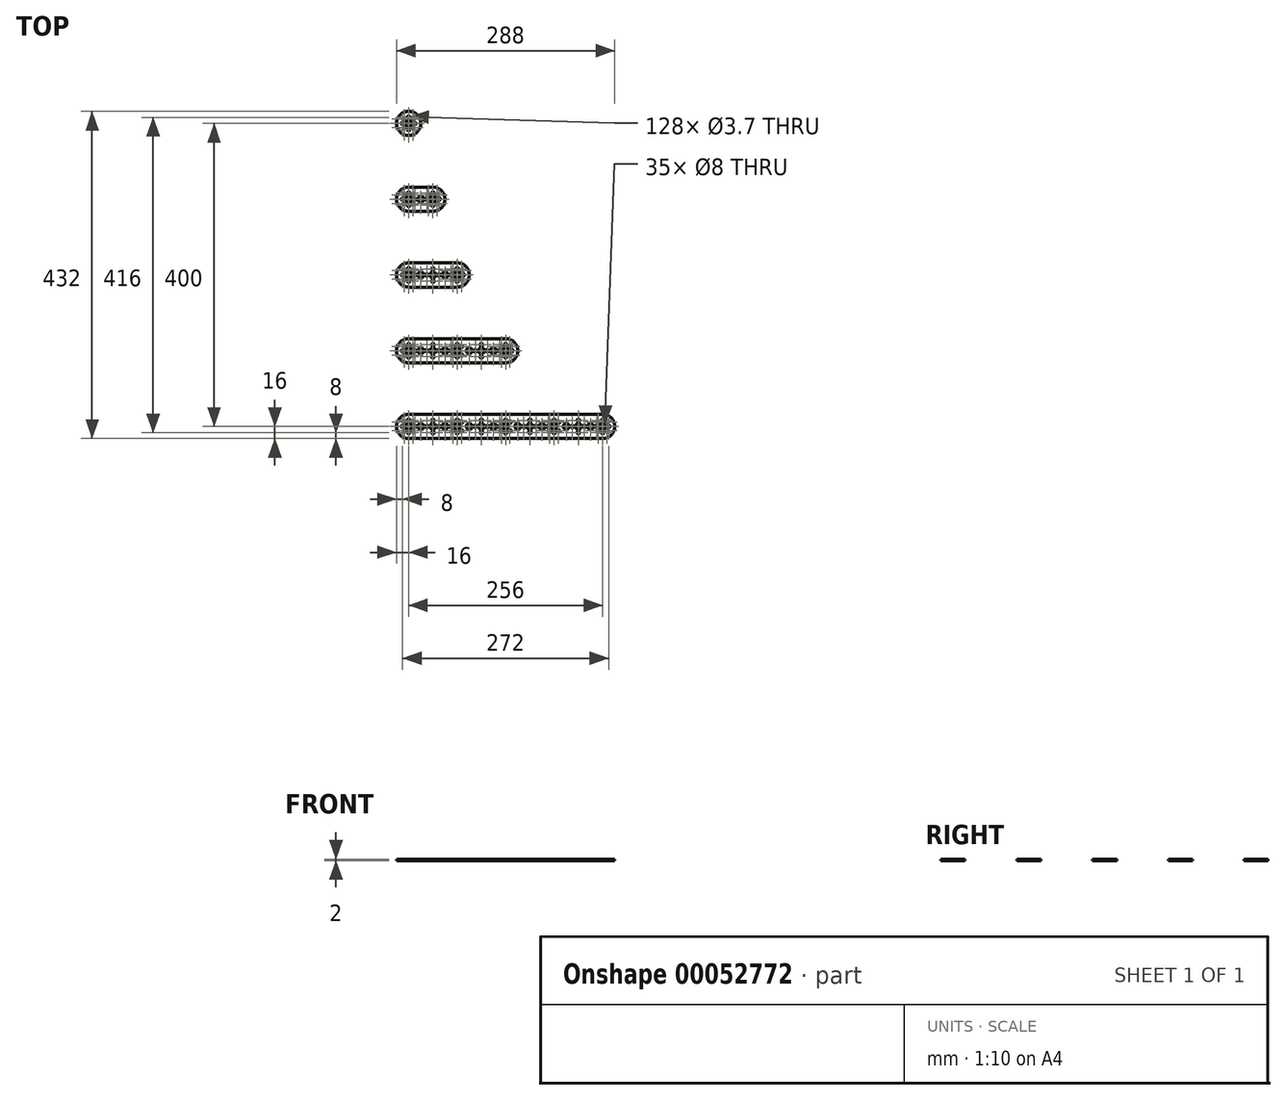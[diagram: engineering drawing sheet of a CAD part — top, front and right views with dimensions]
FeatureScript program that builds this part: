
annotation { "Feature Type Name" : "Feature", "Feature Type Description" : "" }
export const myFeature = defineFeature(function(context is Context, id is Id, definition is map)
    precondition{}
    {
        {
            var Q0;
            Q0=qCreatedBy(makeId("Top.planeOp"),FACE);
            var sketch = newSketch(context, id + "F0", { "sketchPlane" : qUnion([Q0])});
            skCircle(sketch, "E0", {"center": v(0, 0) * mm, "radius": 16 * mm});
            skLineSegment(sketch, "E1", {"start": v(0, 16) * mm, "end": v(32, 16) * mm});
            skCircle(sketch, "E2", {"center": v(32, 0) * mm, "radius": 16 * mm});
            skLineSegment(sketch, "E3", {"start": v(0, -16) * mm, "end": v(32, -16) * mm});
            skSolve(sketch);
        }
        {
            var Q0;
            Q0 = qSketchRegion(id + "F0", true);
            extrude(context, id + "F1", {"entities" : qUnion([Q0]), "depth" : 2 * mm});
        }
        {
            var Q0;
            Q0=makeQuery(id+"F1.opExtrude","CAP_FACE",FACE,{"disambiguationData":[OSD([sQuery(id+"F0.wireOp",EDGE,"E0"),sQuery(id+"F0.wireOp",EDGE,"E1"),sQuery(id+"F0.wireOp",EDGE,"E2"),sQuery(id+"F0.wireOp",EDGE,"E3")])],"isStart":false});
            var sketch = newSketch(context, id + "F2", { "sketchPlane" : qUnion([Q0])});
            skLineSegment(sketch, "E4", {"start": v(32, 0) * mm, "end": v(0, 0) * mm, "construction": true});
            skCircle(sketch, "E5", {"center": v(16, 0) * mm, "radius": 4 * mm});
            skCircle(sketch, "E6", {"center": v(24, 0) * mm, "radius": 1.85 * mm});
            skCircle(sketch, "E7", {"center": v(8, 0) * mm, "radius": 1.85 * mm});
            skCircle(sketch, "E8", {"center": v(32, 0) * mm, "radius": 4 * mm});
            skCircle(sketch, "E9", {"center": v(0, 0) * mm, "radius": 4 * mm});
            skCircle(sketch, "E10.1.0", {"center": v(26.34, -5.66) * mm, "radius": 1.85 * mm});
            skCircle(sketch, "E10.2.0", {"center": v(32, -8) * mm, "radius": 1.85 * mm});
            skCircle(sketch, "E10.3.0", {"center": v(37.66, -5.66) * mm, "radius": 1.85 * mm});
            skCircle(sketch, "E10.4.0", {"center": v(40, 0) * mm, "radius": 1.85 * mm});
            skCircle(sketch, "E10.5.0", {"center": v(37.66, 5.66) * mm, "radius": 1.85 * mm});
            skCircle(sketch, "E10.6.0", {"center": v(32, 8) * mm, "radius": 1.85 * mm});
            skCircle(sketch, "E10.7.0", {"center": v(26.34, 5.66) * mm, "radius": 1.85 * mm});
            skCircle(sketch, "E11.1.0", {"center": v(5.66, 5.66) * mm, "radius": 1.85 * mm});
            skCircle(sketch, "E11.2.0", {"center": v(0, 8) * mm, "radius": 1.85 * mm});
            skCircle(sketch, "E11.3.0", {"center": v(-5.66, 5.66) * mm, "radius": 1.85 * mm});
            skCircle(sketch, "E11.4.0", {"center": v(-8, 0) * mm, "radius": 1.85 * mm});
            skCircle(sketch, "E11.5.0", {"center": v(-5.66, -5.66) * mm, "radius": 1.85 * mm});
            skCircle(sketch, "E11.6.0", {"center": v(0, -8) * mm, "radius": 1.85 * mm});
            skCircle(sketch, "E11.7.0", {"center": v(5.66, -5.66) * mm, "radius": 1.85 * mm});
            skSolve(sketch);
        }
        {
            var Q0;
            Q0=sQuery(id+"F2.wireOp",VERTEX,"E8.center");
            var Q1;
            Q1=sQuery(id+"F2.wireOp",VERTEX,"E5.center");
            var Q2;
            Q2=sQuery(id+"F2.wireOp",VERTEX,"E9.center");
            var Q3;
            Q3=makeQuery(id+"F1.opExtrude","SWEPT_BODY",BODY,{"disambiguationData":[OSD([sQuery(id+"F0.wireOp",EDGE,"E0"),sQuery(id+"F0.wireOp",EDGE,"E1"),sQuery(id+"F0.wireOp",EDGE,"E2"),sQuery(id+"F0.wireOp",EDGE,"E3")])]});
            hole(context, id + "F3", {"style" : HoleStyle.SIMPLE, "holeDiameter" : 8 * mm, "endStyle" : HoleEndStyle.THROUGH, "locations" : qUnion([Q0, Q1, Q2]), "scope" : qUnion([Q3])});
        }
        {
            var Q0;
            Q0=sQuery(id+"F2.wireOp",VERTEX,"E10.3.0.center");
            var Q1;
            Q1=sQuery(id+"F2.wireOp",VERTEX,"E10.2.0.center");
            var Q2;
            Q2=sQuery(id+"F2.wireOp",VERTEX,"E10.1.0.center");
            var Q3;
            Q3=sQuery(id+"F2.wireOp",VERTEX,"E6.center");
            var Q4;
            Q4=sQuery(id+"F2.wireOp",VERTEX,"E10.7.0.center");
            var Q5;
            Q5=sQuery(id+"F2.wireOp",VERTEX,"E10.6.0.center");
            var Q6;
            Q6=sQuery(id+"F2.wireOp",VERTEX,"E10.5.0.center");
            var Q7;
            Q7=sQuery(id+"F2.wireOp",VERTEX,"E4.start");
            var Q8;
            Q8=sQuery(id+"F2.wireOp",VERTEX,"E7.center");
            var Q9;
            Q9=sQuery(id+"F2.wireOp",VERTEX,"E11.1.0.center");
            var Q10;
            Q10=sQuery(id+"F2.wireOp",VERTEX,"E11.2.0.center");
            var Q11;
            Q11=sQuery(id+"F2.wireOp",VERTEX,"E11.3.0.center");
            var Q12;
            Q12=sQuery(id+"F2.wireOp",VERTEX,"E4.end");
            var Q13;
            Q13=sQuery(id+"F2.wireOp",VERTEX,"E11.5.0.center");
            var Q14;
            Q14=sQuery(id+"F2.wireOp",VERTEX,"E11.6.0.center");
            var Q15;
            Q15=sQuery(id+"F2.wireOp",VERTEX,"E11.7.0.center");
            var Q16;
            Q16=sQuery(id+"F2.wireOp",VERTEX,"E10.4.0.center");
            var Q17;
            Q17=sQuery(id+"F2.wireOp",VERTEX,"E11.4.0.center");
            var Q18;
            Q18=makeQuery(id+"F1.opExtrude","SWEPT_BODY",BODY,{"disambiguationData":[OSD([sQuery(id+"F0.wireOp",EDGE,"E0"),sQuery(id+"F0.wireOp",EDGE,"E1"),sQuery(id+"F0.wireOp",EDGE,"E2"),sQuery(id+"F0.wireOp",EDGE,"E3")])]});
            hole(context, id + "F4", {"style" : HoleStyle.SIMPLE, "holeDiameter" : 3.7 * mm, "endStyle" : HoleEndStyle.THROUGH, "locations" : qUnion([Q0, Q1, Q2, Q3, Q4, Q5, Q6, Q7, Q8, Q9, Q10, Q11, Q12, Q13, Q14, Q15, Q16, Q17]), "scope" : qUnion([Q18])});
        }
        {
            var Q0;
            Q0=makeQuery(id+"F1.opExtrude","CAP_FACE",FACE,{"disambiguationData":[OSD([sQuery(id+"F0.wireOp",EDGE,"E0"),sQuery(id+"F0.wireOp",EDGE,"E1"),sQuery(id+"F0.wireOp",EDGE,"E2"),sQuery(id+"F0.wireOp",EDGE,"E3")])],"isStart":true});
            var sketch = newSketch(context, id + "F5", { "sketchPlane" : qUnion([Q0])});
            skLineSegment(sketch, "E12", {"start": v(0, 0) * mm, "end": v(0, -100) * mm});
            skCircle(sketch, "E13", {"center": v(0, -100) * mm, "radius": 16 * mm});
            skSolve(sketch);
        }
        {
            var Q0;
            Q0 = qSketchRegion(id + "F5", true);
            extrude(context, id + "F6", {"entities" : qUnion([Q0]), "oppositeDirection" : true, "depth" : 2 * mm});
        }
        {
            var Q0;
            Q0=makeQuery(id+"F6.opExtrude","CAP_FACE",FACE,{"disambiguationData":[OSD([sQuery(id+"F5.wireOp",EDGE,"E13")])],"isStart":false});
            var sketch = newSketch(context, id + "F7", { "sketchPlane" : qUnion([Q0])});
            skCircle(sketch, "E14", {"center": v(0, 100) * mm, "radius": 4 * mm});
            skLineSegment(sketch, "E15", {"start": v(0, 100) * mm, "end": v(0, 116) * mm, "construction": true});
            skCircle(sketch, "E16", {"center": v(0, 108) * mm, "radius": 1.85 * mm});
            skCircle(sketch, "E17.1.0", {"center": v(-5.66, 105.66) * mm, "radius": 1.85 * mm});
            skCircle(sketch, "E17.2.0", {"center": v(-8, 100) * mm, "radius": 1.85 * mm});
            skCircle(sketch, "E17.3.0", {"center": v(-5.66, 94.34) * mm, "radius": 1.85 * mm});
            skCircle(sketch, "E18.1.4.0", {"center": v(0, 92) * mm, "radius": 1.85 * mm});
            skCircle(sketch, "E18.1.5.0", {"center": v(5.66, 94.34) * mm, "radius": 1.85 * mm});
            skCircle(sketch, "E18.1.6.0", {"center": v(8, 100) * mm, "radius": 1.85 * mm});
            skCircle(sketch, "E18.1.7.0", {"center": v(5.66, 105.66) * mm, "radius": 1.85 * mm});
            skSolve(sketch);
        }
        {
            var Q0;
            Q0=sQuery(id+"F7.wireOp",VERTEX,"E16.center");
            var Q1;
            Q1=sQuery(id+"F7.wireOp",VERTEX,"E18.1.7.0.center");
            var Q2;
            Q2=sQuery(id+"F7.wireOp",VERTEX,"E18.1.6.0.center");
            var Q3;
            Q3=sQuery(id+"F7.wireOp",VERTEX,"E18.1.5.0.center");
            var Q4;
            Q4=sQuery(id+"F7.wireOp",VERTEX,"E18.1.4.0.center");
            var Q5;
            Q5=sQuery(id+"F7.wireOp",VERTEX,"E17.1.0.center");
            var Q6;
            Q6=sQuery(id+"F7.wireOp",VERTEX,"E17.2.0.center");
            var Q7;
            Q7=sQuery(id+"F7.wireOp",VERTEX,"E17.3.0.center");
            var Q8;
            Q8=makeQuery(id+"F6.opExtrude","SWEPT_BODY",BODY,{"disambiguationData":[OSD([sQuery(id+"F5.wireOp",EDGE,"E13")])]});
            hole(context, id + "F8", {"style" : HoleStyle.SIMPLE, "holeDiameter" : 3.7 * mm, "endStyle" : HoleEndStyle.THROUGH, "locations" : qUnion([Q0, Q1, Q2, Q3, Q4, Q5, Q6, Q7]), "scope" : qUnion([Q8])});
        }
        {
            var Q0;
            Q0=sQuery(id+"F7.wireOp",VERTEX,"E14.center");
            var Q1;
            Q1=makeQuery(id+"F6.opExtrude","SWEPT_BODY",BODY,{"disambiguationData":[OSD([sQuery(id+"F5.wireOp",EDGE,"E13")])]});
            hole(context, id + "F9", {"style" : HoleStyle.SIMPLE, "holeDiameter" : 8 * mm, "endStyle" : HoleEndStyle.THROUGH, "locations" : qUnion([Q0]), "scope" : qUnion([Q1])});
        }
        {
            var Q0;
            Q0=makeQuery(id+"F1.opExtrude","CAP_FACE",FACE,{"disambiguationData":[OSD([sQuery(id+"F0.wireOp",EDGE,"E0"),sQuery(id+"F0.wireOp",EDGE,"E1"),sQuery(id+"F0.wireOp",EDGE,"E2"),sQuery(id+"F0.wireOp",EDGE,"E3")])],"isStart":true});
            var sketch = newSketch(context, id + "F10", { "sketchPlane" : qUnion([Q0])});
            skLineSegment(sketch, "E19", {"start": v(0, 0) * mm, "end": v(0, 100) * mm});
            skCircle(sketch, "E20", {"center": v(0, 100) * mm, "radius": 16 * mm});
            skCircle(sketch, "E21", {"center": v(64, 100) * mm, "radius": 16 * mm});
            skLineSegment(sketch, "E22", {"start": v(0, 116) * mm, "end": v(64, 116) * mm});
            skLineSegment(sketch, "E23", {"start": v(0, 84) * mm, "end": v(64, 84) * mm});
            skSolve(sketch);
        }
        {
            var Q0;
            Q0 = qSketchRegion(id + "F10", true);
            extrude(context, id + "F11", {"entities" : qUnion([Q0]), "oppositeDirection" : true, "depth" : 2 * mm});
        }
        {
            var Q0;
            Q0=makeQuery(id+"F11.opExtrude","CAP_FACE",FACE,{"disambiguationData":[OSD([sQuery(id+"F10.wireOp",EDGE,"E20"),sQuery(id+"F10.wireOp",EDGE,"E21"),sQuery(id+"F10.wireOp",EDGE,"E22"),sQuery(id+"F10.wireOp",EDGE,"E23")])],"isStart":false});
            var sketch = newSketch(context, id + "F12", { "sketchPlane" : qUnion([Q0])});
            skCircle(sketch, "E24", {"center": v(0, -100) * mm, "radius": 4 * mm});
            skCircle(sketch, "E25", {"center": v(64, -100) * mm, "radius": 4 * mm});
            skCircle(sketch, "E26", {"center": v(-8, -100) * mm, "radius": 1.85 * mm});
            skCircle(sketch, "E27.1.0", {"center": v(-5.66, -105.66) * mm, "radius": 1.85 * mm});
            skCircle(sketch, "E27.2.0", {"center": v(0, -108) * mm, "radius": 1.85 * mm});
            skCircle(sketch, "E27.3.0", {"center": v(5.66, -105.66) * mm, "radius": 1.85 * mm});
            skCircle(sketch, "E27.4.0", {"center": v(8, -100) * mm, "radius": 1.85 * mm});
            skCircle(sketch, "E27.5.0", {"center": v(5.66, -94.34) * mm, "radius": 1.85 * mm});
            skCircle(sketch, "E27.6.0", {"center": v(0, -92) * mm, "radius": 1.85 * mm});
            skCircle(sketch, "E27.7.0", {"center": v(-5.66, -94.34) * mm, "radius": 1.85 * mm});
            skCircle(sketch, "E28", {"center": v(16, -100) * mm, "radius": 4 * mm});
            skCircle(sketch, "E29", {"center": v(24, -100) * mm, "radius": 1.85 * mm});
            skCircle(sketch, "E30", {"center": v(32, -100) * mm, "radius": 4 * mm});
            skCircle(sketch, "E31.1.0", {"center": v(32, -108) * mm, "radius": 1.85 * mm});
            skCircle(sketch, "E31.2.0", {"center": v(40, -100) * mm, "radius": 1.85 * mm});
            skCircle(sketch, "E31.3.0", {"center": v(32, -92) * mm, "radius": 1.85 * mm});
            skCircle(sketch, "E32", {"center": v(48, -100) * mm, "radius": 4 * mm});
            skCircle(sketch, "E33", {"center": v(56, -100) * mm, "radius": 1.85 * mm});
            skCircle(sketch, "E34.1.0", {"center": v(58.34, -105.66) * mm, "radius": 1.85 * mm});
            skCircle(sketch, "E34.2.0", {"center": v(64, -108) * mm, "radius": 1.85 * mm});
            skCircle(sketch, "E34.3.0", {"center": v(69.66, -105.66) * mm, "radius": 1.85 * mm});
            skCircle(sketch, "E34.4.0", {"center": v(72, -100) * mm, "radius": 1.85 * mm});
            skCircle(sketch, "E34.5.0", {"center": v(69.66, -94.34) * mm, "radius": 1.85 * mm});
            skCircle(sketch, "E34.6.0", {"center": v(64, -92) * mm, "radius": 1.85 * mm});
            skCircle(sketch, "E34.7.0", {"center": v(58.34, -94.34) * mm, "radius": 1.85 * mm});
            skSolve(sketch);
        }
        {
            var Q0;
            Q0=sQuery(id+"F12.wireOp",VERTEX,"E24.center");
            var Q1;
            Q1=sQuery(id+"F12.wireOp",VERTEX,"E28.center");
            var Q2;
            Q2=sQuery(id+"F12.wireOp",VERTEX,"E30.center");
            var Q3;
            Q3=sQuery(id+"F12.wireOp",VERTEX,"E25.center");
            var Q4;
            Q4=sQuery(id+"F12.wireOp",VERTEX,"E32.center");
            var Q5;
            Q5=makeQuery(id+"F11.opExtrude","SWEPT_BODY",BODY,{"disambiguationData":[OSD([sQuery(id+"F10.wireOp",EDGE,"E20"),sQuery(id+"F10.wireOp",EDGE,"E21"),sQuery(id+"F10.wireOp",EDGE,"E22"),sQuery(id+"F10.wireOp",EDGE,"E23")])]});
            hole(context, id + "F13", {"style" : HoleStyle.SIMPLE, "holeDiameter" : 8 * mm, "endStyle" : HoleEndStyle.THROUGH, "locations" : qUnion([Q0, Q1, Q2, Q3, Q4]), "scope" : qUnion([Q5])});
        }
        {
            var Q0;
            Q0=sQuery(id+"F12.wireOp",VERTEX,"E27.7.0.center");
            var Q1;
            Q1=sQuery(id+"F12.wireOp",VERTEX,"E27.6.0.center");
            var Q2;
            Q2=sQuery(id+"F12.wireOp",VERTEX,"E27.5.0.center");
            var Q3;
            Q3=sQuery(id+"F12.wireOp",VERTEX,"E27.4.0.center");
            var Q4;
            Q4=sQuery(id+"F12.wireOp",VERTEX,"E27.3.0.center");
            var Q5;
            Q5=sQuery(id+"F12.wireOp",VERTEX,"E27.2.0.center");
            var Q6;
            Q6=sQuery(id+"F12.wireOp",VERTEX,"E27.1.0.center");
            var Q7;
            Q7=sQuery(id+"F12.wireOp",VERTEX,"E26.center");
            var Q8;
            Q8=sQuery(id+"F12.wireOp",VERTEX,"E29.center");
            var Q9;
            Q9=sQuery(id+"F12.wireOp",VERTEX,"E31.3.0.center");
            var Q10;
            Q10=sQuery(id+"F12.wireOp",VERTEX,"E31.1.0.center");
            var Q11;
            Q11=sQuery(id+"F12.wireOp",VERTEX,"E31.2.0.center");
            var Q12;
            Q12=sQuery(id+"F12.wireOp",VERTEX,"E33.center");
            var Q13;
            Q13=sQuery(id+"F12.wireOp",VERTEX,"E34.1.0.center");
            var Q14;
            Q14=sQuery(id+"F12.wireOp",VERTEX,"E34.2.0.center");
            var Q15;
            Q15=sQuery(id+"F12.wireOp",VERTEX,"E34.3.0.center");
            var Q16;
            Q16=sQuery(id+"F12.wireOp",VERTEX,"E34.4.0.center");
            var Q17;
            Q17=sQuery(id+"F12.wireOp",VERTEX,"E34.5.0.center");
            var Q18;
            Q18=sQuery(id+"F12.wireOp",VERTEX,"E34.6.0.center");
            var Q19;
            Q19=sQuery(id+"F12.wireOp",VERTEX,"E34.7.0.center");
            var Q20;
            Q20=makeQuery(id+"F11.opExtrude","SWEPT_BODY",BODY,{"disambiguationData":[OSD([sQuery(id+"F10.wireOp",EDGE,"E20"),sQuery(id+"F10.wireOp",EDGE,"E21"),sQuery(id+"F10.wireOp",EDGE,"E22"),sQuery(id+"F10.wireOp",EDGE,"E23")])]});
            hole(context, id + "F14", {"style" : HoleStyle.SIMPLE, "holeDiameter" : 3.7 * mm, "endStyle" : HoleEndStyle.THROUGH, "locations" : qUnion([Q0, Q1, Q2, Q3, Q4, Q5, Q6, Q7, Q8, Q9, Q10, Q11, Q12, Q13, Q14, Q15, Q16, Q17, Q18, Q19]), "scope" : qUnion([Q20])});
        }
        {
            var Q0;
            Q0=makeQuery(id+"F11.opExtrude","CAP_FACE",FACE,{"disambiguationData":[OSD([sQuery(id+"F10.wireOp",EDGE,"E20"),sQuery(id+"F10.wireOp",EDGE,"E21"),sQuery(id+"F10.wireOp",EDGE,"E22"),sQuery(id+"F10.wireOp",EDGE,"E23")])],"isStart":true});
            var sketch = newSketch(context, id + "F15", { "sketchPlane" : qUnion([Q0])});
            skLineSegment(sketch, "E35", {"start": v(0, 100) * mm, "end": v(0, 200) * mm});
            skCircle(sketch, "E36", {"center": v(0, 200) * mm, "radius": 16 * mm});
            skCircle(sketch, "E37", {"center": v(128, 200) * mm, "radius": 16 * mm});
            skLineSegment(sketch, "E38", {"start": v(0, 216) * mm, "end": v(128, 216) * mm});
            skLineSegment(sketch, "E39", {"start": v(0, 184) * mm, "end": v(128, 184) * mm});
            skSolve(sketch);
        }
        {
            var Q0;
            {var subQ0=sQuery(id+"F15.wireOp",EDGE,"E38");Q0=makeQuery(id+"F15.imprint","IMPRINT",FACE,{"disambiguationData":[TD([[makeQuery(id+"F15.imprint","IMPRINT",EDGE,{"derivedFrom":subQ0}),-1.0]])]});}
            var Q1;
            {var subQ0=sQuery(id+"F15.wireOp",EDGE,"E36");var subQ1=makeQuery(id+"F15.imprint","INTERSECT",VERTEX,{"derivedFrom":[subQ0,sQuery(id+"F15.wireOp",EDGE,"E38")]});Q1=makeQuery(id+"F15.imprint","IMPRINT",FACE,{"disambiguationData":[TD([[makeQuery(id+"F15.imprint","IMPRINT",EDGE,{"disambiguationData":[TD([[subQ1,-1.0]])],"derivedFrom":subQ0}),1.0]])]});}
            var Q2;
            {var subQ0=sQuery(id+"F15.wireOp",EDGE,"E37");var subQ1=makeQuery(id+"F15.imprint","INTERSECT",VERTEX,{"derivedFrom":[subQ0,sQuery(id+"F15.wireOp",EDGE,"E38")]});Q2=makeQuery(id+"F15.imprint","IMPRINT",FACE,{"disambiguationData":[TD([[makeQuery(id+"F15.imprint","IMPRINT",EDGE,{"disambiguationData":[TD([[subQ1,-1.0]])],"derivedFrom":subQ0}),1.0]])]});}
            extrude(context, id + "F16", {"entities" : qUnion([Q0, Q1, Q2]), "oppositeDirection" : true, "depth" : 2 * mm});
        }
        {
            var Q0;
            Q0=makeQuery(id+"F16.opExtrude","CAP_FACE",FACE,{"disambiguationData":[OSD([sQuery(id+"F15.wireOp",EDGE,"E36"),sQuery(id+"F15.wireOp",EDGE,"E37"),sQuery(id+"F15.wireOp",EDGE,"E38"),sQuery(id+"F15.wireOp",EDGE,"E39")])],"isStart":false});
            var sketch = newSketch(context, id + "F17", { "sketchPlane" : qUnion([Q0])});
            skPoint(sketch, "E40.center", {"position": v(32, -200) * mm});
            skPoint(sketch, "E41.center", {"position": v(0, -200) * mm});
            skCircle(sketch, "E42", {"center": v(16, -200) * mm, "radius": 4 * mm});
            skPoint(sketch, "E43.center", {"position": v(64, -200) * mm});
            skCircle(sketch, "E44", {"center": v(-8, -200) * mm, "radius": 1.85 * mm});
            skCircle(sketch, "E43.6.0", {"center": v(64, -192) * mm, "radius": 1.85 * mm});
            skCircle(sketch, "E40.2.0", {"center": v(40, -200) * mm, "radius": 1.85 * mm});
            skCircle(sketch, "E40.1.0", {"center": v(32, -208) * mm, "radius": 1.85 * mm});
            skCircle(sketch, "E45", {"center": v(56, -200) * mm, "radius": 1.85 * mm});
            skCircle(sketch, "E40.3.0", {"center": v(32, -192) * mm, "radius": 1.85 * mm});
            skCircle(sketch, "E46", {"center": v(64, -200) * mm, "radius": 4 * mm});
            skCircle(sketch, "E43.4.0", {"center": v(72, -200) * mm, "radius": 1.85 * mm});
            skCircle(sketch, "E43.2.0", {"center": v(64, -208) * mm, "radius": 1.85 * mm});
            skCircle(sketch, "E41.7.0", {"center": v(-5.66, -194.34) * mm, "radius": 1.85 * mm});
            skCircle(sketch, "E47", {"center": v(32, -200) * mm, "radius": 4 * mm});
            skCircle(sketch, "E48", {"center": v(24, -200) * mm, "radius": 1.85 * mm});
            skCircle(sketch, "E41.1.0", {"center": v(-5.66, -205.66) * mm, "radius": 1.85 * mm});
            skCircle(sketch, "E41.3.0", {"center": v(5.66, -205.66) * mm, "radius": 1.85 * mm});
            skCircle(sketch, "E41.2.0", {"center": v(0, -208) * mm, "radius": 1.85 * mm});
            skCircle(sketch, "E43.7.0", {"center": v(58.34, -194.34) * mm, "radius": 1.85 * mm});
            skCircle(sketch, "E41.4.0", {"center": v(8, -200) * mm, "radius": 1.85 * mm});
            skCircle(sketch, "E41.6.0", {"center": v(0, -192) * mm, "radius": 1.85 * mm});
            skCircle(sketch, "E41.5.0", {"center": v(5.66, -194.34) * mm, "radius": 1.85 * mm});
            skCircle(sketch, "E43.1.0", {"center": v(58.34, -205.66) * mm, "radius": 1.85 * mm});
            skCircle(sketch, "E49", {"center": v(48, -200) * mm, "radius": 4 * mm});
            skCircle(sketch, "E43.5.0", {"center": v(69.66, -194.34) * mm, "radius": 1.85 * mm});
            skCircle(sketch, "E43.3.0", {"center": v(69.66, -205.66) * mm, "radius": 1.85 * mm});
            skCircle(sketch, "E50", {"center": v(0, -200) * mm, "radius": 4 * mm});
            skArc(sketch, "E51.0", {"start": v(0, -216) * mm, "mid": v(-16, -200) * mm, "end": v(0, -184) * mm});
            skPoint(sketch, "E52.center", {"position": v(96, -200) * mm});
            skCircle(sketch, "E53", {"center": v(80, -200) * mm, "radius": 4 * mm});
            skPoint(sketch, "E54.center", {"position": v(128, -200) * mm});
            skCircle(sketch, "E54.6.0", {"center": v(128, -192) * mm, "radius": 1.85 * mm});
            skCircle(sketch, "E52.2.0", {"center": v(104, -200) * mm, "radius": 1.85 * mm});
            skCircle(sketch, "E52.1.0", {"center": v(96, -208) * mm, "radius": 1.85 * mm});
            skCircle(sketch, "E55", {"center": v(120, -200) * mm, "radius": 1.85 * mm});
            skCircle(sketch, "E52.3.0", {"center": v(96, -192) * mm, "radius": 1.85 * mm});
            skCircle(sketch, "E56", {"center": v(128, -200) * mm, "radius": 4 * mm});
            skCircle(sketch, "E54.4.0", {"center": v(136, -200) * mm, "radius": 1.85 * mm});
            skCircle(sketch, "E54.2.0", {"center": v(128, -208) * mm, "radius": 1.85 * mm});
            skCircle(sketch, "E57", {"center": v(96, -200) * mm, "radius": 4 * mm});
            skCircle(sketch, "E58", {"center": v(88, -200) * mm, "radius": 1.85 * mm});
            skCircle(sketch, "E54.7.0", {"center": v(122.34, -194.34) * mm, "radius": 1.85 * mm});
            skCircle(sketch, "E54.1.0", {"center": v(122.34, -205.66) * mm, "radius": 1.85 * mm});
            skCircle(sketch, "E59", {"center": v(112, -200) * mm, "radius": 4 * mm});
            skCircle(sketch, "E54.5.0", {"center": v(133.66, -194.34) * mm, "radius": 1.85 * mm});
            skCircle(sketch, "E54.3.0", {"center": v(133.66, -205.66) * mm, "radius": 1.85 * mm});
            skSolve(sketch);
        }
        {
            var Q0;
            Q0=sQuery(id+"F17.wireOp",VERTEX,"E41.center");
            var Q1;
            Q1=sQuery(id+"F17.wireOp",VERTEX,"E42.center");
            var Q2;
            Q2=sQuery(id+"F17.wireOp",VERTEX,"E40.center");
            var Q3;
            Q3=sQuery(id+"F17.wireOp",VERTEX,"E49.center");
            var Q4;
            Q4=sQuery(id+"F17.wireOp",VERTEX,"E43.center");
            var Q5;
            Q5=sQuery(id+"F17.wireOp",VERTEX,"E53.center");
            var Q6;
            Q6=sQuery(id+"F17.wireOp",VERTEX,"E52.center");
            var Q7;
            Q7=sQuery(id+"F17.wireOp",VERTEX,"E59.center");
            var Q8;
            Q8=sQuery(id+"F17.wireOp",VERTEX,"E54.center");
            var Q9;
            Q9=makeQuery(id+"F16.opExtrude","SWEPT_BODY",BODY,{"disambiguationData":[OSD([sQuery(id+"F15.wireOp",EDGE,"E36"),sQuery(id+"F15.wireOp",EDGE,"E37"),sQuery(id+"F15.wireOp",EDGE,"E38"),sQuery(id+"F15.wireOp",EDGE,"E39")])]});
            hole(context, id + "F18", {"style" : HoleStyle.SIMPLE, "holeDiameter" : 8 * mm, "endStyle" : HoleEndStyle.THROUGH, "locations" : qUnion([Q0, Q1, Q2, Q3, Q4, Q5, Q6, Q7, Q8]), "scope" : qUnion([Q9])});
        }
        {
            var Q0;
            Q0=sQuery(id+"F17.wireOp",VERTEX,"E41.6.0.center");
            var Q1;
            Q1=sQuery(id+"F17.wireOp",VERTEX,"E41.5.0.center");
            var Q2;
            Q2=sQuery(id+"F17.wireOp",VERTEX,"E41.4.0.center");
            var Q3;
            Q3=sQuery(id+"F17.wireOp",VERTEX,"E41.3.0.center");
            var Q4;
            Q4=sQuery(id+"F17.wireOp",VERTEX,"E41.2.0.center");
            var Q5;
            Q5=sQuery(id+"F17.wireOp",VERTEX,"E41.1.0.center");
            var Q6;
            Q6=sQuery(id+"F17.wireOp",VERTEX,"E44.center");
            var Q7;
            Q7=sQuery(id+"F17.wireOp",VERTEX,"E41.7.0.center");
            var Q8;
            Q8=sQuery(id+"F17.wireOp",VERTEX,"E48.center");
            var Q9;
            Q9=sQuery(id+"F17.wireOp",VERTEX,"E40.3.0.center");
            var Q10;
            Q10=sQuery(id+"F17.wireOp",VERTEX,"E40.2.0.center");
            var Q11;
            Q11=sQuery(id+"F17.wireOp",VERTEX,"E40.1.0.center");
            var Q12;
            Q12=sQuery(id+"F17.wireOp",VERTEX,"E43.7.0.center");
            var Q13;
            Q13=sQuery(id+"F17.wireOp",VERTEX,"E43.6.0.center");
            var Q14;
            Q14=sQuery(id+"F17.wireOp",VERTEX,"E43.5.0.center");
            var Q15;
            Q15=sQuery(id+"F17.wireOp",VERTEX,"E43.4.0.center");
            var Q16;
            Q16=sQuery(id+"F17.wireOp",VERTEX,"E43.3.0.center");
            var Q17;
            Q17=sQuery(id+"F17.wireOp",VERTEX,"E43.2.0.center");
            var Q18;
            Q18=sQuery(id+"F17.wireOp",VERTEX,"E43.1.0.center");
            var Q19;
            Q19=sQuery(id+"F17.wireOp",VERTEX,"E45.center");
            var Q20;
            Q20=sQuery(id+"F17.wireOp",VERTEX,"E58.center");
            var Q21;
            Q21=sQuery(id+"F17.wireOp",VERTEX,"E52.3.0.center");
            var Q22;
            Q22=sQuery(id+"F17.wireOp",VERTEX,"E52.2.0.center");
            var Q23;
            Q23=sQuery(id+"F17.wireOp",VERTEX,"E52.1.0.center");
            var Q24;
            Q24=sQuery(id+"F17.wireOp",VERTEX,"E55.center");
            var Q25;
            Q25=sQuery(id+"F17.wireOp",VERTEX,"E54.7.0.center");
            var Q26;
            Q26=sQuery(id+"F17.wireOp",VERTEX,"E54.6.0.center");
            var Q27;
            Q27=sQuery(id+"F17.wireOp",VERTEX,"E54.5.0.center");
            var Q28;
            Q28=sQuery(id+"F17.wireOp",VERTEX,"E54.4.0.center");
            var Q29;
            Q29=sQuery(id+"F17.wireOp",VERTEX,"E54.3.0.center");
            var Q30;
            Q30=sQuery(id+"F17.wireOp",VERTEX,"E54.2.0.center");
            var Q31;
            Q31=sQuery(id+"F17.wireOp",VERTEX,"E54.1.0.center");
            var Q32;
            Q32=makeQuery(id+"F16.opExtrude","SWEPT_BODY",BODY,{"disambiguationData":[OSD([sQuery(id+"F15.wireOp",EDGE,"E36"),sQuery(id+"F15.wireOp",EDGE,"E37"),sQuery(id+"F15.wireOp",EDGE,"E38"),sQuery(id+"F15.wireOp",EDGE,"E39")])]});
            hole(context, id + "F19", {"style" : HoleStyle.SIMPLE, "holeDiameter" : 3.7 * mm, "endStyle" : HoleEndStyle.THROUGH, "locations" : qUnion([Q0, Q1, Q2, Q3, Q4, Q5, Q6, Q7, Q8, Q9, Q10, Q11, Q12, Q13, Q14, Q15, Q16, Q17, Q18, Q19, Q20, Q21, Q22, Q23, Q24, Q25, Q26, Q27, Q28, Q29, Q30, Q31]), "scope" : qUnion([Q32])});
        }
        {
            var Q0;
            Q0=makeQuery(id+"F16.opExtrude","CAP_FACE",FACE,{"disambiguationData":[OSD([sQuery(id+"F15.wireOp",EDGE,"E36"),sQuery(id+"F15.wireOp",EDGE,"E37"),sQuery(id+"F15.wireOp",EDGE,"E38"),sQuery(id+"F15.wireOp",EDGE,"E39")])],"isStart":true});
            var sketch = newSketch(context, id + "F20", { "sketchPlane" : qUnion([Q0])});
            skLineSegment(sketch, "E60", {"start": v(0, 200) * mm, "end": v(0, 300) * mm});
            skCircle(sketch, "E61", {"center": v(0, 300) * mm, "radius": 16 * mm});
            skCircle(sketch, "E62", {"center": v(256, 300) * mm, "radius": 16 * mm});
            skLineSegment(sketch, "E63", {"start": v(0, 284) * mm, "end": v(256, 284) * mm});
            skLineSegment(sketch, "E64", {"start": v(0, 316) * mm, "end": v(256, 316) * mm});
            skSolve(sketch);
        }
        {
            var Q0;
            Q0 = qSketchRegion(id + "F20", true);
            extrude(context, id + "F21", {"entities" : qUnion([Q0]), "oppositeDirection" : true, "depth" : 2 * mm});
        }
        {
            var Q0;
            Q0=makeQuery(id+"F21.opExtrude","CAP_FACE",FACE,{"disambiguationData":[OSD([sQuery(id+"F20.wireOp",EDGE,"E61"),sQuery(id+"F20.wireOp",EDGE,"E62"),sQuery(id+"F20.wireOp",EDGE,"E63"),sQuery(id+"F20.wireOp",EDGE,"E64")])],"isStart":false});
            var sketch = newSketch(context, id + "F22", { "sketchPlane" : qUnion([Q0])});
            skPoint(sketch, "E65.center", {"position": v(128, -300) * mm});
            skPoint(sketch, "E66.center", {"position": v(32, -300) * mm});
            skPoint(sketch, "E67.center", {"position": v(0, -300) * mm});
            skPoint(sketch, "E68.center", {"position": v(64, -300) * mm});
            skPoint(sketch, "E69.center", {"position": v(96, -300) * mm});
            skCircle(sketch, "E65.4.0", {"center": v(136, -300) * mm, "radius": 1.85 * mm});
            skCircle(sketch, "E70", {"center": v(16, -300) * mm, "radius": 4 * mm});
            skCircle(sketch, "E68.6.0", {"center": v(64, -292) * mm, "radius": 1.85 * mm});
            skCircle(sketch, "E66.1.0", {"center": v(32, -308) * mm, "radius": 1.85 * mm});
            skCircle(sketch, "E67.5.0", {"center": v(5.66, -294.34) * mm, "radius": 1.85 * mm});
            skCircle(sketch, "E66.3.0", {"center": v(32, -292) * mm, "radius": 1.85 * mm});
            skCircle(sketch, "E68.2.0", {"center": v(64, -308) * mm, "radius": 1.85 * mm});
            skCircle(sketch, "E65.2.0", {"center": v(128, -308) * mm, "radius": 1.85 * mm});
            skCircle(sketch, "E68.1.0", {"center": v(58.34, -305.66) * mm, "radius": 1.85 * mm});
            skCircle(sketch, "E68.3.0", {"center": v(69.66, -305.66) * mm, "radius": 1.85 * mm});
            skCircle(sketch, "E65.6.0", {"center": v(128, -292) * mm, "radius": 1.85 * mm});
            skCircle(sketch, "E65.3.0", {"center": v(133.66, -305.66) * mm, "radius": 1.85 * mm});
            skCircle(sketch, "E69.1.0", {"center": v(96, -308) * mm, "radius": 1.85 * mm});
            skCircle(sketch, "E67.4.0", {"center": v(8, -300) * mm, "radius": 1.85 * mm});
            skCircle(sketch, "E71", {"center": v(128, -300) * mm, "radius": 4 * mm});
            skCircle(sketch, "E68.7.0", {"center": v(58.34, -294.34) * mm, "radius": 1.85 * mm});
            skCircle(sketch, "E67.2.0", {"center": v(0, -308) * mm, "radius": 1.85 * mm});
            skCircle(sketch, "E66.2.0", {"center": v(40, -300) * mm, "radius": 1.85 * mm});
            skCircle(sketch, "E67.1.0", {"center": v(-5.66, -305.66) * mm, "radius": 1.85 * mm});
            skCircle(sketch, "E72", {"center": v(24, -300) * mm, "radius": 1.85 * mm});
            skCircle(sketch, "E73", {"center": v(32, -300) * mm, "radius": 4 * mm});
            skCircle(sketch, "E74", {"center": v(96, -300) * mm, "radius": 4 * mm});
            skCircle(sketch, "E75", {"center": v(56, -300) * mm, "radius": 1.85 * mm});
            skCircle(sketch, "E76", {"center": v(64, -300) * mm, "radius": 4 * mm});
            skCircle(sketch, "E67.6.0", {"center": v(0, -292) * mm, "radius": 1.85 * mm});
            skCircle(sketch, "E65.7.0", {"center": v(122.34, -294.34) * mm, "radius": 1.85 * mm});
            skCircle(sketch, "E77", {"center": v(48, -300) * mm, "radius": 4 * mm});
            skCircle(sketch, "E78", {"center": v(88, -300) * mm, "radius": 1.85 * mm});
            skCircle(sketch, "E68.5.0", {"center": v(69.66, -294.34) * mm, "radius": 1.85 * mm});
            skCircle(sketch, "E65.1.0", {"center": v(122.34, -305.66) * mm, "radius": 1.85 * mm});
            skCircle(sketch, "E65.5.0", {"center": v(133.66, -294.34) * mm, "radius": 1.85 * mm});
            skCircle(sketch, "E79", {"center": v(112, -300) * mm, "radius": 4 * mm});
            skCircle(sketch, "E69.2.0", {"center": v(104, -300) * mm, "radius": 1.85 * mm});
            skCircle(sketch, "E80", {"center": v(120, -300) * mm, "radius": 1.85 * mm});
            skCircle(sketch, "E69.3.0", {"center": v(96, -292) * mm, "radius": 1.85 * mm});
            skCircle(sketch, "E67.3.0", {"center": v(5.66, -305.66) * mm, "radius": 1.85 * mm});
            skCircle(sketch, "E81", {"center": v(-8, -300) * mm, "radius": 1.85 * mm});
            skCircle(sketch, "E67.7.0", {"center": v(-5.66, -294.34) * mm, "radius": 1.85 * mm});
            skCircle(sketch, "E82", {"center": v(0, -300) * mm, "radius": 4 * mm});
            skCircle(sketch, "E83", {"center": v(80, -300) * mm, "radius": 4 * mm});
            skCircle(sketch, "E68.4.0", {"center": v(72, -300) * mm, "radius": 1.85 * mm});
            skArc(sketch, "E84.0", {"start": v(0, -316) * mm, "mid": v(-16, -300) * mm, "end": v(0, -284) * mm});
            skPoint(sketch, "E85.center", {"position": v(256, -300) * mm});
            skPoint(sketch, "E86.center", {"position": v(160, -300) * mm});
            skPoint(sketch, "E87.center", {"position": v(192, -300) * mm});
            skPoint(sketch, "E88.center", {"position": v(224, -300) * mm});
            skCircle(sketch, "E85.4.0", {"center": v(264, -300) * mm, "radius": 1.85 * mm});
            skCircle(sketch, "E89", {"center": v(144, -300) * mm, "radius": 4 * mm});
            skCircle(sketch, "E87.6.0", {"center": v(192, -292) * mm, "radius": 1.85 * mm});
            skCircle(sketch, "E86.1.0", {"center": v(160, -308) * mm, "radius": 1.85 * mm});
            skCircle(sketch, "E86.3.0", {"center": v(160, -292) * mm, "radius": 1.85 * mm});
            skCircle(sketch, "E87.2.0", {"center": v(192, -308) * mm, "radius": 1.85 * mm});
            skCircle(sketch, "E85.2.0", {"center": v(256, -308) * mm, "radius": 1.85 * mm});
            skCircle(sketch, "E87.1.0", {"center": v(186.34, -305.66) * mm, "radius": 1.85 * mm});
            skCircle(sketch, "E87.3.0", {"center": v(197.66, -305.66) * mm, "radius": 1.85 * mm});
            skCircle(sketch, "E85.6.0", {"center": v(256, -292) * mm, "radius": 1.85 * mm});
            skCircle(sketch, "E85.3.0", {"center": v(261.66, -305.66) * mm, "radius": 1.85 * mm});
            skCircle(sketch, "E88.1.0", {"center": v(224, -308) * mm, "radius": 1.85 * mm});
            skCircle(sketch, "E90", {"center": v(256, -300) * mm, "radius": 4 * mm});
            skCircle(sketch, "E87.7.0", {"center": v(186.34, -294.34) * mm, "radius": 1.85 * mm});
            skCircle(sketch, "E86.2.0", {"center": v(168, -300) * mm, "radius": 1.85 * mm});
            skCircle(sketch, "E91", {"center": v(152, -300) * mm, "radius": 1.85 * mm});
            skCircle(sketch, "E92", {"center": v(160, -300) * mm, "radius": 4 * mm});
            skCircle(sketch, "E93", {"center": v(224, -300) * mm, "radius": 4 * mm});
            skCircle(sketch, "E94", {"center": v(184, -300) * mm, "radius": 1.85 * mm});
            skCircle(sketch, "E95", {"center": v(192, -300) * mm, "radius": 4 * mm});
            skCircle(sketch, "E85.7.0", {"center": v(250.34, -294.34) * mm, "radius": 1.85 * mm});
            skCircle(sketch, "E96", {"center": v(176, -300) * mm, "radius": 4 * mm});
            skCircle(sketch, "E97", {"center": v(216, -300) * mm, "radius": 1.85 * mm});
            skCircle(sketch, "E87.5.0", {"center": v(197.66, -294.34) * mm, "radius": 1.85 * mm});
            skCircle(sketch, "E85.1.0", {"center": v(250.34, -305.66) * mm, "radius": 1.85 * mm});
            skCircle(sketch, "E85.5.0", {"center": v(261.66, -294.34) * mm, "radius": 1.85 * mm});
            skCircle(sketch, "E98", {"center": v(240, -300) * mm, "radius": 4 * mm});
            skCircle(sketch, "E88.2.0", {"center": v(232, -300) * mm, "radius": 1.85 * mm});
            skCircle(sketch, "E99", {"center": v(248, -300) * mm, "radius": 1.85 * mm});
            skCircle(sketch, "E88.3.0", {"center": v(224, -292) * mm, "radius": 1.85 * mm});
            skCircle(sketch, "E100", {"center": v(208, -300) * mm, "radius": 4 * mm});
            skCircle(sketch, "E87.4.0", {"center": v(200, -300) * mm, "radius": 1.85 * mm});
            skSolve(sketch);
        }
        {
            var Q0;
            Q0=sQuery(id+"F22.wireOp",VERTEX,"E67.center");
            var Q1;
            Q1=sQuery(id+"F22.wireOp",VERTEX,"E70.center");
            var Q2;
            Q2=sQuery(id+"F22.wireOp",VERTEX,"E66.center");
            var Q3;
            Q3=sQuery(id+"F22.wireOp",VERTEX,"E77.center");
            var Q4;
            Q4=sQuery(id+"F22.wireOp",VERTEX,"E68.center");
            var Q5;
            Q5=sQuery(id+"F22.wireOp",VERTEX,"E83.center");
            var Q6;
            Q6=sQuery(id+"F22.wireOp",VERTEX,"E69.center");
            var Q7;
            Q7=sQuery(id+"F22.wireOp",VERTEX,"E79.center");
            var Q8;
            Q8=sQuery(id+"F22.wireOp",VERTEX,"E65.center");
            var Q9;
            Q9=sQuery(id+"F22.wireOp",VERTEX,"E89.center");
            var Q10;
            Q10=sQuery(id+"F22.wireOp",VERTEX,"E86.center");
            var Q11;
            Q11=sQuery(id+"F22.wireOp",VERTEX,"E96.center");
            var Q12;
            Q12=sQuery(id+"F22.wireOp",VERTEX,"E87.center");
            var Q13;
            Q13=sQuery(id+"F22.wireOp",VERTEX,"E100.center");
            var Q14;
            Q14=sQuery(id+"F22.wireOp",VERTEX,"E88.center");
            var Q15;
            Q15=sQuery(id+"F22.wireOp",VERTEX,"E98.center");
            var Q16;
            Q16=sQuery(id+"F22.wireOp",VERTEX,"E85.center");
            var Q17;
            Q17=makeQuery(id+"F21.opExtrude","SWEPT_BODY",BODY,{"disambiguationData":[OSD([sQuery(id+"F20.wireOp",EDGE,"E61"),sQuery(id+"F20.wireOp",EDGE,"E62"),sQuery(id+"F20.wireOp",EDGE,"E63"),sQuery(id+"F20.wireOp",EDGE,"E64")])]});
            hole(context, id + "F23", {"style" : HoleStyle.SIMPLE, "holeDiameter" : 8 * mm, "endStyle" : HoleEndStyle.THROUGH, "locations" : qUnion([Q0, Q1, Q2, Q3, Q4, Q5, Q6, Q7, Q8, Q9, Q10, Q11, Q12, Q13, Q14, Q15, Q16]), "scope" : qUnion([Q17])});
        }
        {
            var Q0;
            Q0=sQuery(id+"F22.wireOp",VERTEX,"E67.6.0.center");
            var Q1;
            Q1=sQuery(id+"F22.wireOp",VERTEX,"E67.5.0.center");
            var Q2;
            Q2=sQuery(id+"F22.wireOp",VERTEX,"E67.4.0.center");
            var Q3;
            Q3=sQuery(id+"F22.wireOp",VERTEX,"E67.3.0.center");
            var Q4;
            Q4=sQuery(id+"F22.wireOp",VERTEX,"E67.2.0.center");
            var Q5;
            Q5=sQuery(id+"F22.wireOp",VERTEX,"E67.1.0.center");
            var Q6;
            Q6=sQuery(id+"F22.wireOp",VERTEX,"E81.center");
            var Q7;
            Q7=sQuery(id+"F22.wireOp",VERTEX,"E67.7.0.center");
            var Q8;
            Q8=sQuery(id+"F22.wireOp",VERTEX,"E72.center");
            var Q9;
            Q9=sQuery(id+"F22.wireOp",VERTEX,"E66.3.0.center");
            var Q10;
            Q10=sQuery(id+"F22.wireOp",VERTEX,"E66.1.0.center");
            var Q11;
            Q11=sQuery(id+"F22.wireOp",VERTEX,"E66.2.0.center");
            var Q12;
            Q12=sQuery(id+"F22.wireOp",VERTEX,"E68.7.0.center");
            var Q13;
            Q13=sQuery(id+"F22.wireOp",VERTEX,"E75.center");
            var Q14;
            Q14=sQuery(id+"F22.wireOp",VERTEX,"E68.1.0.center");
            var Q15;
            Q15=sQuery(id+"F22.wireOp",VERTEX,"E68.2.0.center");
            var Q16;
            Q16=sQuery(id+"F22.wireOp",VERTEX,"E68.4.0.center");
            var Q17;
            Q17=sQuery(id+"F22.wireOp",VERTEX,"E68.3.0.center");
            var Q18;
            Q18=sQuery(id+"F22.wireOp",VERTEX,"E68.5.0.center");
            var Q19;
            Q19=sQuery(id+"F22.wireOp",VERTEX,"E68.6.0.center");
            var Q20;
            Q20=sQuery(id+"F22.wireOp",VERTEX,"E78.center");
            var Q21;
            Q21=sQuery(id+"F22.wireOp",VERTEX,"E69.3.0.center");
            var Q22;
            Q22=sQuery(id+"F22.wireOp",VERTEX,"E69.2.0.center");
            var Q23;
            Q23=sQuery(id+"F22.wireOp",VERTEX,"E69.1.0.center");
            var Q24;
            Q24=sQuery(id+"F22.wireOp",VERTEX,"E80.center");
            var Q25;
            Q25=sQuery(id+"F22.wireOp",VERTEX,"E65.7.0.center");
            var Q26;
            Q26=sQuery(id+"F22.wireOp",VERTEX,"E65.6.0.center");
            var Q27;
            Q27=sQuery(id+"F22.wireOp",VERTEX,"E65.5.0.center");
            var Q28;
            Q28=sQuery(id+"F22.wireOp",VERTEX,"E65.4.0.center");
            var Q29;
            Q29=sQuery(id+"F22.wireOp",VERTEX,"E65.3.0.center");
            var Q30;
            Q30=sQuery(id+"F22.wireOp",VERTEX,"E65.2.0.center");
            var Q31;
            Q31=sQuery(id+"F22.wireOp",VERTEX,"E65.1.0.center");
            var Q32;
            Q32=sQuery(id+"F22.wireOp",VERTEX,"E91.center");
            var Q33;
            Q33=sQuery(id+"F22.wireOp",VERTEX,"E86.3.0.center");
            var Q34;
            Q34=sQuery(id+"F22.wireOp",VERTEX,"E86.2.0.center");
            var Q35;
            Q35=sQuery(id+"F22.wireOp",VERTEX,"E86.1.0.center");
            var Q36;
            Q36=sQuery(id+"F22.wireOp",VERTEX,"E94.center");
            var Q37;
            Q37=sQuery(id+"F22.wireOp",VERTEX,"E87.7.0.center");
            var Q38;
            Q38=sQuery(id+"F22.wireOp",VERTEX,"E87.6.0.center");
            var Q39;
            Q39=sQuery(id+"F22.wireOp",VERTEX,"E87.5.0.center");
            var Q40;
            Q40=sQuery(id+"F22.wireOp",VERTEX,"E87.4.0.center");
            var Q41;
            Q41=sQuery(id+"F22.wireOp",VERTEX,"E87.3.0.center");
            var Q42;
            Q42=sQuery(id+"F22.wireOp",VERTEX,"E87.2.0.center");
            var Q43;
            Q43=sQuery(id+"F22.wireOp",VERTEX,"E87.1.0.center");
            var Q44;
            Q44=sQuery(id+"F22.wireOp",VERTEX,"E97.center");
            var Q45;
            Q45=sQuery(id+"F22.wireOp",VERTEX,"E88.3.0.center");
            var Q46;
            Q46=sQuery(id+"F22.wireOp",VERTEX,"E88.1.0.center");
            var Q47;
            Q47=sQuery(id+"F22.wireOp",VERTEX,"E88.2.0.center");
            var Q48;
            Q48=sQuery(id+"F22.wireOp",VERTEX,"E99.center");
            var Q49;
            Q49=sQuery(id+"F22.wireOp",VERTEX,"E85.7.0.center");
            var Q50;
            Q50=sQuery(id+"F22.wireOp",VERTEX,"E85.6.0.center");
            var Q51;
            Q51=sQuery(id+"F22.wireOp",VERTEX,"E85.5.0.center");
            var Q52;
            Q52=sQuery(id+"F22.wireOp",VERTEX,"E85.4.0.center");
            var Q53;
            Q53=sQuery(id+"F22.wireOp",VERTEX,"E85.3.0.center");
            var Q54;
            Q54=sQuery(id+"F22.wireOp",VERTEX,"E85.2.0.center");
            var Q55;
            Q55=sQuery(id+"F22.wireOp",VERTEX,"E85.1.0.center");
            var Q56;
            Q56=makeQuery(id+"F21.opExtrude","SWEPT_BODY",BODY,{"disambiguationData":[OSD([sQuery(id+"F20.wireOp",EDGE,"E61"),sQuery(id+"F20.wireOp",EDGE,"E62"),sQuery(id+"F20.wireOp",EDGE,"E63"),sQuery(id+"F20.wireOp",EDGE,"E64")])]});
            hole(context, id + "F24", {"style" : HoleStyle.SIMPLE, "holeDiameter" : 3.7 * mm, "endStyle" : HoleEndStyle.THROUGH, "locations" : qUnion([Q0, Q1, Q2, Q3, Q4, Q5, Q6, Q7, Q8, Q9, Q10, Q11, Q12, Q13, Q14, Q15, Q16, Q17, Q18, Q19, Q20, Q21, Q22, Q23, Q24, Q25, Q26, Q27, Q28, Q29, Q30, Q31, Q32, Q33, Q34, Q35, Q36, Q37, Q38, Q39, Q40, Q41, Q42, Q43, Q44, Q45, Q46, Q47, Q48, Q49, Q50, Q51, Q52, Q53, Q54, Q55]), "scope" : qUnion([Q56])});
        }
    });
